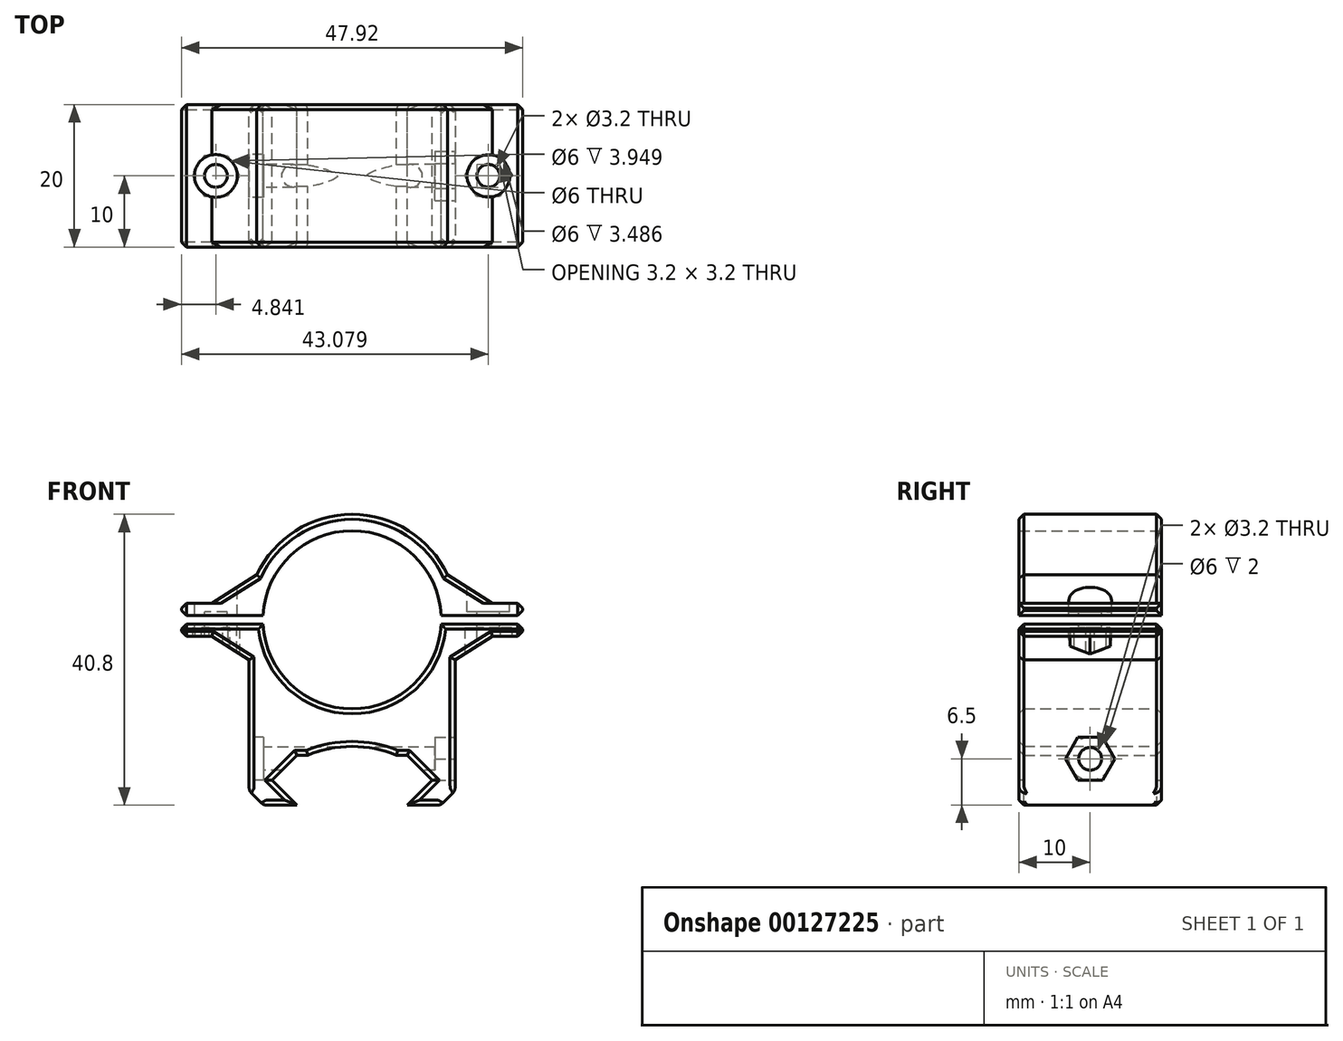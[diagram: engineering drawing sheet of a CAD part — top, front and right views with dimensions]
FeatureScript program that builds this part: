
annotation { "Feature Type Name" : "Feature", "Feature Type Description" : "" }
export const myFeature = defineFeature(function(context is Context, id is Id, definition is map)
    precondition{}
    {
        {
            var Q0;
            Q0=qCreatedBy(makeId("Front.planeOp"),FACE);
            var sketch = newSketch(context, id + "F0", { "sketchPlane" : qUnion([Q0])});
            skArc(sketch, "E0", {"start": v(0, -14.8) * mm, "mid": v(10.25, -10.67) * mm, "end": v(14.79, -0.6) * mm});
            skLineSegment(sketch, "E1.bottom", {"start": v(14.62, 2.3) * mm, "end": v(23.96, 2.3) * mm});
            skLineSegment(sketch, "E1.top", {"start": v(14.62, -2.3) * mm, "end": v(23.96, -2.3) * mm});
            skLineSegment(sketch, "E1.right", {"start": v(23.96, 2.3) * mm, "end": v(23.96, 0.6) * mm});
            skLineSegment(sketch, "E2", {"start": v(-7.75, -26) * mm, "end": v(-11.25, -22.5) * mm});
            skLineSegment(sketch, "E3.0", {"start": v(-14.45, -26) * mm, "end": v(-14.45, -14.6) * mm});
            skLineSegment(sketch, "E4.MirrorCS", {"start": v(7.75, -26) * mm, "end": v(11.25, -22.5) * mm});
            skLineSegment(sketch, "E5.MirrorCS", {"start": v(14.45, -26) * mm, "end": v(14.45, -23.8) * mm});
            skLineSegment(sketch, "E6.bottom", {"start": v(23.96, 0.6) * mm, "end": v(14.62, 0.6) * mm});
            skLineSegment(sketch, "E6.top", {"start": v(23.96, -0.6) * mm, "end": v(14.62, -0.6) * mm});
            skPoint(sketch, "E6.middle", {"position": v(19.29, 0) * mm});
            skLineSegment(sketch, "E7", {"start": v(-14.45, -3.2) * mm, "end": v(-14.45, -14.6) * mm});
            skLineSegment(sketch, "E8", {"start": v(14.45, -3.2) * mm, "end": v(14.45, -23.8) * mm});
            skLineSegment(sketch, "E9", {"start": v(-14.45, -26) * mm, "end": v(-7.75, -26) * mm});
            skLineSegment(sketch, "E10", {"start": v(7.75, -26) * mm, "end": v(14.45, -26) * mm});
            skLineSegment(sketch, "E11.trimOffspring", {"start": v(23.96, -0.6) * mm, "end": v(23.96, -2.3) * mm});
            skLineSegment(sketch, "E12", {"start": v(-7.75, -19) * mm, "end": v(-11.25, -22.5) * mm});
            skLineSegment(sketch, "E13.MirrorCS", {"start": v(7.75, -19) * mm, "end": v(11.25, -22.5) * mm});
            skArc(sketch, "E14", {"start": v(12.49, 0.6) * mm, "mid": v(-12.5, 0) * mm, "end": v(12.49, -0.6) * mm});
            skLineSegment(sketch, "E15", {"start": v(-7.75, -19) * mm, "end": v(0, -19) * mm});
            skLineSegment(sketch, "E16", {"start": v(0, -19) * mm, "end": v(0, -14.8) * mm});
            skLineSegment(sketch, "E17", {"start": v(7.75, -19) * mm, "end": v(0, -19) * mm});
            skLineSegment(sketch, "E18", {"start": v(0, -14.8) * mm, "end": v(0, -14.8) * mm});
            skLineSegment(sketch, "E19", {"start": v(14.62, 2.3) * mm, "end": v(12.29, 2.3) * mm});
            skLineSegment(sketch, "E20", {"start": v(14.62, 0.6) * mm, "end": v(12.49, 0.6) * mm});
            skLineSegment(sketch, "E21", {"start": v(14.62, -0.6) * mm, "end": v(12.49, -0.6) * mm});
            skLineSegment(sketch, "E22", {"start": v(14.62, -2.3) * mm, "end": v(12.29, -2.3) * mm});
            skArc(sketch, "E23.trimOffspring", {"start": v(14.79, 0.6) * mm, "mid": v(-10.67, 10.25) * mm, "end": v(0, -14.8) * mm});
            skLineSegment(sketch, "E24.MirrorCS", {"start": v(-14.62, 2.3) * mm, "end": v(-23.96, 2.3) * mm});
            skLineSegment(sketch, "E25.MirrorCS", {"start": v(-23.96, 2.3) * mm, "end": v(-23.96, 0.6) * mm});
            skLineSegment(sketch, "E26.MirrorCS", {"start": v(-23.96, 0.6) * mm, "end": v(-14.62, 0.6) * mm});
            skLineSegment(sketch, "E27.MirrorCS", {"start": v(-23.96, -0.6) * mm, "end": v(-14.62, -0.6) * mm});
            skLineSegment(sketch, "E28.MirrorCS", {"start": v(-14.62, -2.3) * mm, "end": v(-23.96, -2.3) * mm});
            skLineSegment(sketch, "E29.MirrorCS", {"start": v(-23.96, -0.6) * mm, "end": v(-23.96, -2.3) * mm});
            skLineSegment(sketch, "E30.MirrorCS", {"start": v(-14.62, 0.6) * mm, "end": v(-12.49, 0.6) * mm});
            skLineSegment(sketch, "E31.MirrorCS", {"start": v(-14.62, -0.6) * mm, "end": v(-12.49, -0.6) * mm});
            skPoint(sketch, "E32.orphan", {"position": v(14.45, -14.6) * mm});
            skArc(sketch, "E33", {"start": v(6.25, -19) * mm, "mid": v(0, -17.77) * mm, "end": v(-6.25, -19) * mm});
            skSolve(sketch);
        }
        {
            var Q0;
            Q0=makeQuery(id+"F0.imprint","IMPRINT",FACE,{"disambiguationData":[TD([[makeQuery(id+"F0.imprint","IMPRINT",EDGE,{"derivedFrom":sQuery(id+"F0.wireOp",EDGE,"E2")}),1.0]])]});
            var Q1;
            Q1=makeQuery(id+"F0.imprint","IMPRINT",FACE,{"disambiguationData":[TD([[makeQuery(id+"F0.imprint","IMPRINT",EDGE,{"derivedFrom":sQuery(id+"F0.wireOp",EDGE,"W4pV5Rjo-NDwQ-rgVk-bVmp-dATyTHXsbS4B")}),-1.0]])]});
            var Q2;
            Q2=makeQuery(id+"F0.imprint","IMPRINT",FACE,{"disambiguationData":[TD([[makeQuery(id+"F0.imprint","IMPRINT",EDGE,{"derivedFrom":sQuery(id+"F0.wireOp",EDGE,"E4.MirrorCS")}),-1.0]])]});
            var Q3;
            {var subQ0=sQuery(id+"F0.wireOp",EDGE,"E1.bottom");Q3=makeQuery(id+"F0.imprint","IMPRINT",FACE,{"disambiguationData":[TD([[makeQuery(id+"F0.imprint","IMPRINT",EDGE,{"derivedFrom":subQ0}),-1.0]])]});}
            var Q4;
            {var subQ0=sQuery(id+"F0.wireOp",EDGE,"E1.top");Q4=makeQuery(id+"F0.imprint","IMPRINT",FACE,{"disambiguationData":[TD([[makeQuery(id+"F0.imprint","IMPRINT",EDGE,{"derivedFrom":subQ0}),1.0]])]});}
            var Q5;
            Q5=makeQuery(id+"F0.imprint","IMPRINT",FACE,{"disambiguationData":[TD([[makeQuery(id+"F0.imprint","IMPRINT",EDGE,{"derivedFrom":sQuery(id+"F0.wireOp",EDGE,"E14")}),-1.0]])]});
            var Q6;
            {var subQ0=sQuery(id+"F0.wireOp",EDGE,"E18");Q6=makeQuery(id+"F0.imprint","IMPRINT",FACE,{"disambiguationData":[TD([[makeQuery(id+"F0.imprint","IMPRINT",EDGE,{"derivedFrom":subQ0}),-1.0]])]});}
            var Q7;
            {var subQ0=sQuery(id+"F0.wireOp",EDGE,"E19");Q7=makeQuery(id+"F0.imprint","IMPRINT",FACE,{"disambiguationData":[TD([[makeQuery(id+"F0.imprint","IMPRINT",EDGE,{"derivedFrom":subQ0}),-1.0]])]});}
            var Q8;
            {var subQ0=sQuery(id+"F0.wireOp",EDGE,"E22");Q8=makeQuery(id+"F0.imprint","IMPRINT",FACE,{"disambiguationData":[TD([[makeQuery(id+"F0.imprint","IMPRINT",EDGE,{"derivedFrom":subQ0}),1.0]])]});}
            var Q9;
            {var subQ0=sQuery(id+"F0.wireOp",EDGE,"E24.MirrorCS");Q9=makeQuery(id+"F0.imprint","IMPRINT",FACE,{"disambiguationData":[TD([[makeQuery(id+"F0.imprint","IMPRINT",EDGE,{"derivedFrom":subQ0}),1.0]])]});}
            var Q10;
            {var subQ0=sQuery(id+"F0.wireOp",EDGE,"E28.MirrorCS");Q10=makeQuery(id+"F0.imprint","IMPRINT",FACE,{"disambiguationData":[TD([[makeQuery(id+"F0.imprint","IMPRINT",EDGE,{"derivedFrom":subQ0}),-1.0]])]});}
            extrude(context, id + "F1", {"entities" : qUnion([Q0, Q1, Q2, Q3, Q4, Q5, Q6, Q7, Q8, Q9, Q10]), "depth" : 20 * mm});
        }
        {
            var Q0;
            Q0=makeQuery(id+"F1.opExtrude","SWEPT_FACE",FACE,{"disambiguationData":[OSD([sQuery(id+"F0.wireOp",EDGE,"E24.MirrorCS")])]});
            var sketch = newSketch(context, id + "F2", { "sketchPlane" : qUnion([Q0])});
            skCircle(sketch, "E34", {"center": v(19.12, -10) * mm, "radius": 1.6 * mm});
            skCircle(sketch, "E35", {"center": v(19.12, -10) * mm, "radius": 3 * mm});
            skCircle(sketch, "E36.MirrorC", {"center": v(-19.12, -10) * mm, "radius": 1.6 * mm});
            skCircle(sketch, "E37.MirrorC", {"center": v(-19.12, -10) * mm, "radius": 3 * mm});
            skLineSegment(sketch, "E38", {"start": v(-19.12, 0) * mm, "end": v(-19.12, -20) * mm, "construction": true});
            skSolve(sketch);
        }
        {
            var Q0;
            Q0=makeQuery(id+"F1.opExtrude","SWEPT_FACE",FACE,{"disambiguationData":[OSD([sQuery(id+"F0.wireOp",EDGE,"E7")])]});
            var sketch = newSketch(context, id + "F3", { "sketchPlane" : qUnion([Q0])});
            skCircle(sketch, "E39", {"center": v(10, -19.5) * mm, "radius": 1.6 * mm});
            skCircle(sketch, "E40", {"center": v(10, -19.5) * mm, "radius": 3 * mm});
            skLineSegment(sketch, "E41", {"start": v(0, -19.5) * mm, "end": v(20, -19.5) * mm});
            skSolve(sketch);
        }
        {
            var Q0;
            Q0=makeQuery(id+"F3.imprint","IMPRINT",FACE,{"disambiguationData":[TD([[makeQuery(id+"F3.imprint","IMPRINT",EDGE,{"derivedFrom":sQuery(id+"F3.wireOp",EDGE,"E39")}),1.0]])]});
            extrude(context, id + "F4", {"entities" : qUnion([Q0]), "operationType" : NewBodyOperationType.REMOVE, "oppositeDirection" : true, "depth" : 40 * mm});
        }
        {
            var Q0;
            Q0=makeQuery(id+"F2.imprint","IMPRINT",FACE,{"disambiguationData":[TD([[makeQuery(id+"F2.imprint","IMPRINT",EDGE,{"derivedFrom":sQuery(id+"F2.wireOp",EDGE,"E34")}),1.0]])]});
            var Q1;
            Q1=makeQuery(id+"F2.imprint","IMPRINT",FACE,{"disambiguationData":[TD([[makeQuery(id+"F2.imprint","IMPRINT",EDGE,{"derivedFrom":sQuery(id+"F2.wireOp",EDGE,"E36.MirrorC")}),-1.0]])]});
            extrude(context, id + "F5", {"entities" : qUnion([Q0, Q1]), "operationType" : NewBodyOperationType.REMOVE, "oppositeDirection" : true, "depth" : 25 * mm});
        }
        {
            var Q0;
            Q0=qSketchRegion(id+"F3",true);
            var Q1;
            {var subQ0=sQuery(id+"F3.wireOp",EDGE,"E41");var subQ1=sQuery(id+"F3.wireOp",EDGE,"E39");var subQ2=makeQuery(id+"F3.imprint","INTERSECT",VERTEX,{"disambiguationData":[OD(0.0)],"derivedFrom":[subQ1,subQ0]});Q1=makeQuery(id+"F3.imprint","IMPRINT",FACE,{"disambiguationData":[TD([[makeQuery(id+"F3.imprint","IMPRINT",EDGE,{"disambiguationData":[TD([[subQ2,1.0]])],"derivedFrom":subQ1}),-1.0]])]});}
            extrude(context, id + "F6", {"entities" : qUnion([Q0, Q1]), "operationType" : NewBodyOperationType.REMOVE, "oppositeDirection" : true, "depth" : 2 * mm});
        }
        {
            var Q0;
            Q0=makeQuery(id+"F1.opExtrude","SWEPT_FACE",FACE,{"disambiguationData":[OSD([sQuery(id+"F0.wireOp",EDGE,"E8")])]});
            var sketch = newSketch(context, id + "F7", { "sketchPlane" : qUnion([Q0])});
            skCircle(sketch, "E42.cCircle", {"center": v(-10, -19.5) * mm, "radius": 3 * mm, "construction": true});
            skLineSegment(sketch, "E42.0", {"start": v(-8.27, -22.5) * mm, "end": v(-11.73, -22.5) * mm});
            skLineSegment(sketch, "E42.1", {"start": v(-11.73, -22.5) * mm, "end": v(-13.46, -19.5) * mm});
            skLineSegment(sketch, "E42.2", {"start": v(-13.46, -19.5) * mm, "end": v(-11.73, -16.5) * mm});
            skLineSegment(sketch, "E42.3", {"start": v(-11.73, -16.5) * mm, "end": v(-8.27, -16.5) * mm});
            skLineSegment(sketch, "E42.4", {"start": v(-8.27, -16.5) * mm, "end": v(-6.54, -19.5) * mm});
            skLineSegment(sketch, "E42.5", {"start": v(-6.54, -19.5) * mm, "end": v(-8.27, -22.5) * mm});
            skPoint(sketch, "E42.0.midPoint", {"position": v(-10, -22.5) * mm});
            skLineSegment(sketch, "E43", {"start": v(-20, -19.5) * mm, "end": v(0, -19.5) * mm, "construction": true});
            skSolve(sketch);
        }
        {
            var Q0;
            Q0=makeQuery(id+"F2.imprint","IMPRINT",FACE,{"disambiguationData":[TD([[makeQuery(id+"F2.imprint","IMPRINT",EDGE,{"derivedFrom":sQuery(id+"F2.wireOp",EDGE,"E34")}),-1.0]])]});
            var Q1;
            Q1=makeQuery(id+"F2.imprint","IMPRINT",FACE,{"disambiguationData":[TD([[makeQuery(id+"F2.imprint","IMPRINT",EDGE,{"derivedFrom":sQuery(id+"F2.wireOp",EDGE,"E36.MirrorC")}),1.0]])]});
            extrude(context, id + "F8", {"entities" : qUnion([Q0, Q1]), "operationType" : NewBodyOperationType.REMOVE, "oppositeDirection" : true, "depth" : 1.2 * mm});
        }
        {
            var Q0;
            Q0=makeQuery(id+"F1.opExtrude","SWEPT_FACE",FACE,{"disambiguationData":[OSD([sQuery(id+"F0.wireOp",EDGE,"E1.top")])]});
            var sketch = newSketch(context, id + "F9", { "sketchPlane" : qUnion([Q0])});
            skCircle(sketch, "E44.cCircle", {"center": v(19.12, 10) * mm, "radius": 2.85 * mm, "construction": true});
            skLineSegment(sketch, "E44.0", {"start": v(20.76, 7.15) * mm, "end": v(17.47, 7.15) * mm});
            skLineSegment(sketch, "E44.1", {"start": v(17.47, 7.15) * mm, "end": v(15.83, 10) * mm});
            skLineSegment(sketch, "E44.2", {"start": v(15.83, 10) * mm, "end": v(17.47, 12.85) * mm});
            skLineSegment(sketch, "E44.3", {"start": v(17.47, 12.85) * mm, "end": v(20.76, 12.85) * mm});
            skLineSegment(sketch, "E44.4", {"start": v(20.76, 12.85) * mm, "end": v(22.4, 10) * mm});
            skLineSegment(sketch, "E44.5", {"start": v(22.4, 10) * mm, "end": v(20.76, 7.15) * mm});
            skPoint(sketch, "E44.0.midPoint", {"position": v(19.12, 7.15) * mm});
            skCircle(sketch, "E45", {"center": v(19.12, 10) * mm, "radius": 1.6 * mm});
            skCircle(sketch, "E46.cCircle", {"center": v(-19.12, 10) * mm, "radius": 2.85 * mm, "construction": true});
            skLineSegment(sketch, "E46.0", {"start": v(-15.83, 10) * mm, "end": v(-17.47, 7.15) * mm});
            skLineSegment(sketch, "E46.1", {"start": v(-17.47, 7.15) * mm, "end": v(-20.76, 7.15) * mm});
            skLineSegment(sketch, "E46.2", {"start": v(-20.76, 7.15) * mm, "end": v(-22.4, 10) * mm});
            skLineSegment(sketch, "E46.3", {"start": v(-22.4, 10) * mm, "end": v(-20.76, 12.85) * mm});
            skLineSegment(sketch, "E46.4", {"start": v(-20.76, 12.85) * mm, "end": v(-17.47, 12.85) * mm});
            skLineSegment(sketch, "E46.5", {"start": v(-17.47, 12.85) * mm, "end": v(-15.83, 10) * mm});
            skPoint(sketch, "E46.0.midPoint", {"position": v(-16.65, 8.57) * mm});
            skLineSegment(sketch, "E47.0", {"start": v(-19.12, 0) * mm, "end": v(-19.12, 20) * mm, "construction": true});
            skSolve(sketch);
        }
        {
            var Q0;
            Q0=makeQuery(id+"F1.opExtrude","SWEPT_EDGE",EDGE,{"disambiguationData":[OSD([sQuery(id+"F0.wireOp",EDGE,"E1.bottom"),sQuery(id+"F0.wireOp",EDGE,"E19"),sQuery(id+"F0.wireOp",EDGE,"E23.trimOffspring")])]});
            var Q1;
            Q1=makeQuery(id+"F1.opExtrude","SWEPT_EDGE",EDGE,{"disambiguationData":[OSD([sQuery(id+"F0.wireOp",EDGE,"E0"),sQuery(id+"F0.wireOp",EDGE,"E1.top"),sQuery(id+"F0.wireOp",EDGE,"E22")])]});
            var Q2;
            Q2=makeQuery(id+"F1.opExtrude","SWEPT_EDGE",EDGE,{"disambiguationData":[OSD([sQuery(id+"F0.wireOp",EDGE,"E23.trimOffspring"),sQuery(id+"F0.wireOp",EDGE,"E24.MirrorCS")])]});
            var Q3;
            Q3=makeQuery(id+"F1.opExtrude","SWEPT_EDGE",EDGE,{"disambiguationData":[OSD([sQuery(id+"F0.wireOp",EDGE,"E23.trimOffspring"),sQuery(id+"F0.wireOp",EDGE,"E28.MirrorCS")])]});
            chamfer(context, id + "F10", {"entities" : qUnion([Q0, Q1, Q2, Q3]), "width" : 7 * mm, "tangentPropagation" : true});
        }
        {
            var Q0;
            Q0=makeQuery(id+"F1.opExtrude","CAP_FACE",FACE,{"disambiguationData":[OSD([sQuery(id+"F0.wireOp",EDGE,"E0"),sQuery(id+"F0.wireOp",EDGE,"E1.bottom"),sQuery(id+"F0.wireOp",EDGE,"E1.top"),sQuery(id+"F0.wireOp",EDGE,"E1.right"),sQuery(id+"F0.wireOp",EDGE,"E2"),sQuery(id+"F0.wireOp",EDGE,"E3.0"),sQuery(id+"F0.wireOp",EDGE,"E4.MirrorCS"),sQuery(id+"F0.wireOp",EDGE,"E5.MirrorCS"),sQuery(id+"F0.wireOp",EDGE,"E6.bottom"),sQuery(id+"F0.wireOp",EDGE,"E6.top"),sQuery(id+"F0.wireOp",EDGE,"E7"),sQuery(id+"F0.wireOp",EDGE,"E8"),sQuery(id+"F0.wireOp",EDGE,"E9"),sQuery(id+"F0.wireOp",EDGE,"E10"),sQuery(id+"F0.wireOp",EDGE,"E11.trimOffspring"),sQuery(id+"F0.wireOp",EDGE,"E12"),sQuery(id+"F0.wireOp",EDGE,"E13.MirrorCS"),sQuery(id+"F0.wireOp",EDGE,"E14"),sQuery(id+"F0.wireOp",EDGE,"E15"),sQuery(id+"F0.wireOp",EDGE,"E17"),sQuery(id+"F0.wireOp",EDGE,"E20"),sQuery(id+"F0.wireOp",EDGE,"E21"),sQuery(id+"F0.wireOp",EDGE,"E23.trimOffspring"),sQuery(id+"F0.wireOp",EDGE,"E24.MirrorCS"),sQuery(id+"F0.wireOp",EDGE,"E25.MirrorCS"),sQuery(id+"F0.wireOp",EDGE,"E26.MirrorCS"),sQuery(id+"F0.wireOp",EDGE,"E27.MirrorCS"),sQuery(id+"F0.wireOp",EDGE,"E28.MirrorCS"),sQuery(id+"F0.wireOp",EDGE,"E29.MirrorCS")])],"isStart":false});
            var sketch = newSketch(context, id + "F11", { "sketchPlane" : qUnion([Q0])});
            skLineSegment(sketch, "E48.bottom", {"start": v(-23.96, 0.6) * mm, "end": v(-20.41, 0.6) * mm});
            skLineSegment(sketch, "E48.top", {"start": v(-23.96, -0.6) * mm, "end": v(-20.41, -0.6) * mm});
            skLineSegment(sketch, "E48.left", {"start": v(-23.96, 0.6) * mm, "end": v(-23.96, -0.6) * mm});
            skLineSegment(sketch, "E48.right", {"start": v(-20.41, 0.6) * mm, "end": v(-20.41, -0.6) * mm});
            skSolve(sketch);
        }
        {
            var Q0;
            {var subQ0=sQuery(id+"F11.wireOp",EDGE,"E48.right");Q0=makeQuery(id+"F11.imprint","IMPRINT",FACE,{"disambiguationData":[TD([[makeQuery(id+"F11.imprint","IMPRINT",EDGE,{"derivedFrom":subQ0}),-1.0]])]});}
            var Q1;
            {var subQ0=sQuery(id+"F11.wireOp",EDGE,"E48.left");Q1=makeQuery(id+"F11.imprint","IMPRINT",FACE,{"disambiguationData":[TD([[makeQuery(id+"F11.imprint","IMPRINT",EDGE,{"derivedFrom":subQ0}),1.0]])]});}
            extrude(context, id + "F12", {"entities" : qUnion([Q0, Q1]), "operationType" : NewBodyOperationType.REMOVE, "endBound" : BoundingType.THROUGH_ALL, "oppositeDirection" : true, "depth" : 25 * mm});
        }
        {
            var Q0;
            Q0=qSketchRegion(id+"F9",true);
            extrude(context, id + "F13", {"entities" : qUnion([Q0]), "operationType" : NewBodyOperationType.REMOVE, "oppositeDirection" : true, "depth" : 1.2 * mm, "hasSecondDirection" : true, "secondDirectionOppositeDirection" : false, "secondDirectionDepth" : 25 * mm});
        }
        {
            var Q0;
            Q0=qSketchRegion(id+"F7",true);
            extrude(context, id + "F14", {"entities" : qUnion([Q0]), "operationType" : NewBodyOperationType.REMOVE, "oppositeDirection" : true, "depth" : 2.8 * mm});
        }
        {
            var Q0;
            Q0=makeQuery(id+"F1.opExtrude","CAP_EDGE",EDGE,{"disambiguationData":[OSD([sQuery(id+"F0.wireOp",EDGE,"E5.MirrorCS"),sQuery(id+"F0.wireOp",EDGE,"E8")])],"isStart":false});
            var Q1;
            {var subQ0=sQuery(id+"F0.wireOp",EDGE,"E33");var subQ1=sQuery(id+"F0.wireOp",EDGE,"E29.MirrorCS");var subQ2=sQuery(id+"F0.wireOp",EDGE,"E28.MirrorCS");var subQ3=sQuery(id+"F0.wireOp",EDGE,"E14");var subQ4=sQuery(id+"F0.wireOp",EDGE,"E17");var subQ5=sQuery(id+"F0.wireOp",EDGE,"E23.trimOffspring");var subQ6=sQuery(id+"F0.wireOp",EDGE,"E7");var subQ7=sQuery(id+"F0.wireOp",EDGE,"E11.trimOffspring");var subQ8=sQuery(id+"F0.wireOp",EDGE,"E12");var subQ9=sQuery(id+"F0.wireOp",EDGE,"E3.0");var subQ10=sQuery(id+"F0.wireOp",EDGE,"E2");var subQ11=sQuery(id+"F0.wireOp",EDGE,"E1.top");var subQ12=sQuery(id+"F0.wireOp",EDGE,"E27.MirrorCS");var subQ13=sQuery(id+"F0.wireOp",EDGE,"E0");var subQ14=sQuery(id+"F0.wireOp",EDGE,"E4.MirrorCS");var subQ15=sQuery(id+"F0.wireOp",EDGE,"E13.MirrorCS");var subQ16=sQuery(id+"F0.wireOp",EDGE,"E8");var subQ17=sQuery(id+"F0.wireOp",EDGE,"E5.MirrorCS");var subQ18=sQuery(id+"F0.wireOp",EDGE,"E15");var subQ19=sQuery(id+"F0.wireOp",EDGE,"E21");var subQ20=sQuery(id+"F0.wireOp",EDGE,"E6.top");var subQ21=sQuery(id+"F0.wireOp",EDGE,"E9");var subQ22=sQuery(id+"F0.wireOp",EDGE,"E10");Q1=makeQuery(id+"F12.boolean.opBoolean","SPLIT",FACE,{"disambiguationData":[TD([makeQuery(id+"F1.opExtrude","SWEPT_FACE",FACE,{"disambiguationData":[OSD([subQ13])]})])],"derivedFrom":makeQuery(id+"F1.opExtrude","CAP_FACE",FACE,{"disambiguationData":[OSD([subQ13,sQuery(id+"F0.wireOp",EDGE,"E1.bottom"),subQ11,sQuery(id+"F0.wireOp",EDGE,"E1.right"),subQ10,subQ9,subQ14,subQ17,sQuery(id+"F0.wireOp",EDGE,"E6.bottom"),subQ20,subQ6,subQ16,subQ21,subQ22,subQ7,subQ8,subQ15,subQ3,subQ18,subQ4,sQuery(id+"F0.wireOp",EDGE,"E20"),subQ19,subQ5,sQuery(id+"F0.wireOp",EDGE,"E24.MirrorCS"),sQuery(id+"F0.wireOp",EDGE,"E25.MirrorCS"),sQuery(id+"F0.wireOp",EDGE,"E26.MirrorCS"),subQ12,subQ2,subQ1,subQ0])],"isStart":false})});}
            var Q2;
            {var subQ0=sQuery(id+"F0.wireOp",EDGE,"E24.MirrorCS");var subQ1=sQuery(id+"F0.wireOp",EDGE,"E23.trimOffspring");var subQ3=sQuery(id+"F0.wireOp",EDGE,"E1.bottom");var subQ4=sQuery(id+"F0.wireOp",EDGE,"E26.MirrorCS");var subQ5=sQuery(id+"F0.wireOp",EDGE,"E25.MirrorCS");var subQ6=sQuery(id+"F0.wireOp",EDGE,"E14");var subQ7=sQuery(id+"F0.wireOp",EDGE,"E20");var subQ8=sQuery(id+"F0.wireOp",EDGE,"E6.bottom");var subQ9=sQuery(id+"F0.wireOp",EDGE,"E1.right");Q2=makeQuery(id+"F12.boolean.opBoolean","SPLIT",FACE,{"disambiguationData":[TD([makeQuery(id+"F1.opExtrude","SWEPT_FACE",FACE,{"disambiguationData":[OSD([subQ3])]})])],"derivedFrom":makeQuery(id+"F1.opExtrude","CAP_FACE",FACE,{"disambiguationData":[OSD([sQuery(id+"F0.wireOp",EDGE,"E0"),subQ3,sQuery(id+"F0.wireOp",EDGE,"E1.top"),subQ9,sQuery(id+"F0.wireOp",EDGE,"E2"),sQuery(id+"F0.wireOp",EDGE,"E3.0"),sQuery(id+"F0.wireOp",EDGE,"E4.MirrorCS"),sQuery(id+"F0.wireOp",EDGE,"E5.MirrorCS"),subQ8,sQuery(id+"F0.wireOp",EDGE,"E6.top"),sQuery(id+"F0.wireOp",EDGE,"E7"),sQuery(id+"F0.wireOp",EDGE,"E8"),sQuery(id+"F0.wireOp",EDGE,"E9"),sQuery(id+"F0.wireOp",EDGE,"E10"),sQuery(id+"F0.wireOp",EDGE,"E11.trimOffspring"),sQuery(id+"F0.wireOp",EDGE,"E12"),sQuery(id+"F0.wireOp",EDGE,"E13.MirrorCS"),subQ6,sQuery(id+"F0.wireOp",EDGE,"E15"),sQuery(id+"F0.wireOp",EDGE,"E17"),subQ7,sQuery(id+"F0.wireOp",EDGE,"E21"),subQ1,subQ0,subQ5,subQ4,sQuery(id+"F0.wireOp",EDGE,"E27.MirrorCS"),sQuery(id+"F0.wireOp",EDGE,"E28.MirrorCS"),sQuery(id+"F0.wireOp",EDGE,"E29.MirrorCS"),sQuery(id+"F0.wireOp",EDGE,"E33")])],"isStart":false})});}
            var Q3;
            {var subQ0=sQuery(id+"F0.wireOp",EDGE,"E24.MirrorCS");var subQ1=sQuery(id+"F0.wireOp",EDGE,"E23.trimOffspring");var subQ3=sQuery(id+"F0.wireOp",EDGE,"E1.bottom");var subQ4=sQuery(id+"F0.wireOp",EDGE,"E26.MirrorCS");var subQ5=sQuery(id+"F0.wireOp",EDGE,"E25.MirrorCS");var subQ6=sQuery(id+"F0.wireOp",EDGE,"E14");var subQ7=sQuery(id+"F0.wireOp",EDGE,"E20");var subQ8=sQuery(id+"F0.wireOp",EDGE,"E6.bottom");var subQ9=sQuery(id+"F0.wireOp",EDGE,"E1.right");Q3=makeQuery(id+"F12.boolean.opBoolean","SPLIT",FACE,{"disambiguationData":[TD([makeQuery(id+"F1.opExtrude","SWEPT_FACE",FACE,{"disambiguationData":[OSD([subQ3])]})])],"derivedFrom":makeQuery(id+"F1.opExtrude","CAP_FACE",FACE,{"disambiguationData":[OSD([sQuery(id+"F0.wireOp",EDGE,"E0"),subQ3,sQuery(id+"F0.wireOp",EDGE,"E1.top"),subQ9,sQuery(id+"F0.wireOp",EDGE,"E2"),sQuery(id+"F0.wireOp",EDGE,"E3.0"),sQuery(id+"F0.wireOp",EDGE,"E4.MirrorCS"),sQuery(id+"F0.wireOp",EDGE,"E5.MirrorCS"),subQ8,sQuery(id+"F0.wireOp",EDGE,"E6.top"),sQuery(id+"F0.wireOp",EDGE,"E7"),sQuery(id+"F0.wireOp",EDGE,"E8"),sQuery(id+"F0.wireOp",EDGE,"E9"),sQuery(id+"F0.wireOp",EDGE,"E10"),sQuery(id+"F0.wireOp",EDGE,"E11.trimOffspring"),sQuery(id+"F0.wireOp",EDGE,"E12"),sQuery(id+"F0.wireOp",EDGE,"E13.MirrorCS"),subQ6,sQuery(id+"F0.wireOp",EDGE,"E15"),sQuery(id+"F0.wireOp",EDGE,"E17"),subQ7,sQuery(id+"F0.wireOp",EDGE,"E21"),subQ1,subQ0,subQ5,subQ4,sQuery(id+"F0.wireOp",EDGE,"E27.MirrorCS"),sQuery(id+"F0.wireOp",EDGE,"E28.MirrorCS"),sQuery(id+"F0.wireOp",EDGE,"E29.MirrorCS"),sQuery(id+"F0.wireOp",EDGE,"E33")])],"isStart":true})});}
            var Q4;
            {var subQ0=sQuery(id+"F0.wireOp",EDGE,"E33");var subQ1=sQuery(id+"F0.wireOp",EDGE,"E29.MirrorCS");var subQ2=sQuery(id+"F0.wireOp",EDGE,"E28.MirrorCS");var subQ3=sQuery(id+"F0.wireOp",EDGE,"E14");var subQ4=sQuery(id+"F0.wireOp",EDGE,"E17");var subQ5=sQuery(id+"F0.wireOp",EDGE,"E23.trimOffspring");var subQ6=sQuery(id+"F0.wireOp",EDGE,"E7");var subQ7=sQuery(id+"F0.wireOp",EDGE,"E11.trimOffspring");var subQ8=sQuery(id+"F0.wireOp",EDGE,"E12");var subQ9=sQuery(id+"F0.wireOp",EDGE,"E3.0");var subQ10=sQuery(id+"F0.wireOp",EDGE,"E2");var subQ11=sQuery(id+"F0.wireOp",EDGE,"E1.top");var subQ12=sQuery(id+"F0.wireOp",EDGE,"E27.MirrorCS");var subQ13=sQuery(id+"F0.wireOp",EDGE,"E0");var subQ14=sQuery(id+"F0.wireOp",EDGE,"E4.MirrorCS");var subQ15=sQuery(id+"F0.wireOp",EDGE,"E13.MirrorCS");var subQ16=sQuery(id+"F0.wireOp",EDGE,"E8");var subQ17=sQuery(id+"F0.wireOp",EDGE,"E5.MirrorCS");var subQ18=sQuery(id+"F0.wireOp",EDGE,"E15");var subQ19=sQuery(id+"F0.wireOp",EDGE,"E21");var subQ20=sQuery(id+"F0.wireOp",EDGE,"E6.top");var subQ21=sQuery(id+"F0.wireOp",EDGE,"E9");var subQ22=sQuery(id+"F0.wireOp",EDGE,"E10");Q4=makeQuery(id+"F12.boolean.opBoolean","SPLIT",FACE,{"disambiguationData":[TD([makeQuery(id+"F1.opExtrude","SWEPT_FACE",FACE,{"disambiguationData":[OSD([subQ13])]})])],"derivedFrom":makeQuery(id+"F1.opExtrude","CAP_FACE",FACE,{"disambiguationData":[OSD([subQ13,sQuery(id+"F0.wireOp",EDGE,"E1.bottom"),subQ11,sQuery(id+"F0.wireOp",EDGE,"E1.right"),subQ10,subQ9,subQ14,subQ17,sQuery(id+"F0.wireOp",EDGE,"E6.bottom"),subQ20,subQ6,subQ16,subQ21,subQ22,subQ7,subQ8,subQ15,subQ3,subQ18,subQ4,sQuery(id+"F0.wireOp",EDGE,"E20"),subQ19,subQ5,sQuery(id+"F0.wireOp",EDGE,"E24.MirrorCS"),sQuery(id+"F0.wireOp",EDGE,"E25.MirrorCS"),sQuery(id+"F0.wireOp",EDGE,"E26.MirrorCS"),subQ12,subQ2,subQ1,subQ0])],"isStart":true})});}
            var Q5;
            Q5=makeQuery(id+"F1.opExtrude","SWEPT_FACE",FACE,{"disambiguationData":[OSD([sQuery(id+"F0.wireOp",EDGE,"E1.right")])]});
            var Q6;
            Q6=makeQuery(id+"F1.opExtrude","SWEPT_FACE",FACE,{"disambiguationData":[OSD([sQuery(id+"F0.wireOp",EDGE,"E11.trimOffspring")])]});
            var Q7;
            Q7=makeQuery(id+"F1.opExtrude","SWEPT_FACE",FACE,{"disambiguationData":[OSD([sQuery(id+"F0.wireOp",EDGE,"E25.MirrorCS")])]});
            var Q8;
            Q8=makeQuery(id+"F1.opExtrude","SWEPT_FACE",FACE,{"disambiguationData":[OSD([sQuery(id+"F0.wireOp",EDGE,"E29.MirrorCS")])]});
            var Q9;
            {var subQ0=sQuery(id+"F0.wireOp",EDGE,"E24.MirrorCS");var subQ1=sQuery(id+"F0.wireOp",EDGE,"E23.trimOffspring");Q9=makeQuery(id+"F10.opChamfer","BLEND_EDGE",EDGE,{"blendedFrom":[makeQuery(id+"F1.opExtrude","SWEPT_EDGE",EDGE,{"disambiguationData":[OSD([subQ1,subQ0])]}),makeQuery(id+"F1.opExtrude","CAP_FACE",FACE,{"disambiguationData":[OSD([sQuery(id+"F0.wireOp",EDGE,"E1.bottom"),sQuery(id+"F0.wireOp",EDGE,"E1.right"),sQuery(id+"F0.wireOp",EDGE,"E6.bottom"),sQuery(id+"F0.wireOp",EDGE,"E14"),sQuery(id+"F0.wireOp",EDGE,"E20"),subQ1,subQ0,sQuery(id+"F0.wireOp",EDGE,"E25.MirrorCS"),sQuery(id+"F0.wireOp",EDGE,"E26.MirrorCS"),sQuery(id+"F0.wireOp",EDGE,"E30.MirrorCS")])],"isStart":false})],"blendedInto":[makeQuery(id+"F1.opExtrude","CAP_FACE",FACE,{"disambiguationData":[OSD([sQuery(id+"F0.wireOp",EDGE,"E1.bottom"),sQuery(id+"F0.wireOp",EDGE,"E1.right"),sQuery(id+"F0.wireOp",EDGE,"E6.bottom"),sQuery(id+"F0.wireOp",EDGE,"E14"),sQuery(id+"F0.wireOp",EDGE,"E20"),subQ1,subQ0,sQuery(id+"F0.wireOp",EDGE,"E25.MirrorCS"),sQuery(id+"F0.wireOp",EDGE,"E26.MirrorCS"),sQuery(id+"F0.wireOp",EDGE,"E30.MirrorCS")])],"isStart":false})]});}
            var Q10;
            {var subQ0=sQuery(id+"F0.wireOp",EDGE,"E23.trimOffspring");Q10=makeQuery(id+"F1.opExtrude","CAP_EDGE",EDGE,{"disambiguationData":[OSD([subQ0]),TDD([makeQuery(id+"F0.imprint","IMPRINT",EDGE,{"disambiguationData":[TD([[makeQuery(id+"F0.imprint","INTERSECT",VERTEX,{"derivedFrom":[subQ0,sQuery(id+"F0.wireOp",EDGE,"E24.MirrorCS")]}),1.0]])],"derivedFrom":subQ0})])],"isStart":false});}
            var Q11;
            {var subQ0=sQuery(id+"F0.wireOp",EDGE,"E23.trimOffspring");var subQ1=sQuery(id+"F0.wireOp",EDGE,"E1.bottom");Q11=makeQuery(id+"F10.opChamfer","BLEND_EDGE",EDGE,{"blendedFrom":[makeQuery(id+"F1.opExtrude","SWEPT_EDGE",EDGE,{"disambiguationData":[OSD([subQ1,sQuery(id+"F0.wireOp",EDGE,"E19"),subQ0])]}),makeQuery(id+"F1.opExtrude","CAP_FACE",FACE,{"disambiguationData":[OSD([subQ1,sQuery(id+"F0.wireOp",EDGE,"E1.right"),sQuery(id+"F0.wireOp",EDGE,"E6.bottom"),sQuery(id+"F0.wireOp",EDGE,"E14"),sQuery(id+"F0.wireOp",EDGE,"E20"),subQ0,sQuery(id+"F0.wireOp",EDGE,"E24.MirrorCS"),sQuery(id+"F0.wireOp",EDGE,"E25.MirrorCS"),sQuery(id+"F0.wireOp",EDGE,"E26.MirrorCS"),sQuery(id+"F0.wireOp",EDGE,"E30.MirrorCS")])],"isStart":false})],"blendedInto":[makeQuery(id+"F1.opExtrude","CAP_FACE",FACE,{"disambiguationData":[OSD([subQ1,sQuery(id+"F0.wireOp",EDGE,"E1.right"),sQuery(id+"F0.wireOp",EDGE,"E6.bottom"),sQuery(id+"F0.wireOp",EDGE,"E14"),sQuery(id+"F0.wireOp",EDGE,"E20"),subQ0,sQuery(id+"F0.wireOp",EDGE,"E24.MirrorCS"),sQuery(id+"F0.wireOp",EDGE,"E25.MirrorCS"),sQuery(id+"F0.wireOp",EDGE,"E26.MirrorCS"),sQuery(id+"F0.wireOp",EDGE,"E30.MirrorCS")])],"isStart":false})]});}
            var Q12;
            {var subQ0=sQuery(id+"F0.wireOp",EDGE,"E24.MirrorCS");var subQ1=sQuery(id+"F0.wireOp",EDGE,"E23.trimOffspring");Q12=makeQuery(id+"F10.opChamfer","BLEND_EDGE",EDGE,{"blendedFrom":[makeQuery(id+"F1.opExtrude","SWEPT_EDGE",EDGE,{"disambiguationData":[OSD([subQ1,subQ0])]}),makeQuery(id+"F1.opExtrude","CAP_FACE",FACE,{"disambiguationData":[OSD([sQuery(id+"F0.wireOp",EDGE,"E1.bottom"),sQuery(id+"F0.wireOp",EDGE,"E1.right"),sQuery(id+"F0.wireOp",EDGE,"E6.bottom"),sQuery(id+"F0.wireOp",EDGE,"E14"),sQuery(id+"F0.wireOp",EDGE,"E20"),subQ1,subQ0,sQuery(id+"F0.wireOp",EDGE,"E25.MirrorCS"),sQuery(id+"F0.wireOp",EDGE,"E26.MirrorCS"),sQuery(id+"F0.wireOp",EDGE,"E30.MirrorCS")])],"isStart":true})],"blendedInto":[makeQuery(id+"F1.opExtrude","CAP_FACE",FACE,{"disambiguationData":[OSD([sQuery(id+"F0.wireOp",EDGE,"E1.bottom"),sQuery(id+"F0.wireOp",EDGE,"E1.right"),sQuery(id+"F0.wireOp",EDGE,"E6.bottom"),sQuery(id+"F0.wireOp",EDGE,"E14"),sQuery(id+"F0.wireOp",EDGE,"E20"),subQ1,subQ0,sQuery(id+"F0.wireOp",EDGE,"E25.MirrorCS"),sQuery(id+"F0.wireOp",EDGE,"E26.MirrorCS"),sQuery(id+"F0.wireOp",EDGE,"E30.MirrorCS")])],"isStart":true})]});}
            var Q13;
            {var subQ0=sQuery(id+"F0.wireOp",EDGE,"E23.trimOffspring");Q13=makeQuery(id+"F1.opExtrude","CAP_EDGE",EDGE,{"disambiguationData":[OSD([subQ0]),TDD([makeQuery(id+"F0.imprint","IMPRINT",EDGE,{"disambiguationData":[TD([[makeQuery(id+"F0.imprint","INTERSECT",VERTEX,{"derivedFrom":[subQ0,sQuery(id+"F0.wireOp",EDGE,"E24.MirrorCS")]}),1.0]])],"derivedFrom":subQ0})])],"isStart":true});}
            var Q14;
            {var subQ0=sQuery(id+"F0.wireOp",EDGE,"E23.trimOffspring");var subQ1=sQuery(id+"F0.wireOp",EDGE,"E1.bottom");Q14=makeQuery(id+"F10.opChamfer","BLEND_EDGE",EDGE,{"blendedFrom":[makeQuery(id+"F1.opExtrude","SWEPT_EDGE",EDGE,{"disambiguationData":[OSD([subQ1,sQuery(id+"F0.wireOp",EDGE,"E19"),subQ0])]}),makeQuery(id+"F1.opExtrude","CAP_FACE",FACE,{"disambiguationData":[OSD([subQ1,sQuery(id+"F0.wireOp",EDGE,"E1.right"),sQuery(id+"F0.wireOp",EDGE,"E6.bottom"),sQuery(id+"F0.wireOp",EDGE,"E14"),sQuery(id+"F0.wireOp",EDGE,"E20"),subQ0,sQuery(id+"F0.wireOp",EDGE,"E24.MirrorCS"),sQuery(id+"F0.wireOp",EDGE,"E25.MirrorCS"),sQuery(id+"F0.wireOp",EDGE,"E26.MirrorCS"),sQuery(id+"F0.wireOp",EDGE,"E30.MirrorCS")])],"isStart":true})],"blendedInto":[makeQuery(id+"F1.opExtrude","CAP_FACE",FACE,{"disambiguationData":[OSD([subQ1,sQuery(id+"F0.wireOp",EDGE,"E1.right"),sQuery(id+"F0.wireOp",EDGE,"E6.bottom"),sQuery(id+"F0.wireOp",EDGE,"E14"),sQuery(id+"F0.wireOp",EDGE,"E20"),subQ0,sQuery(id+"F0.wireOp",EDGE,"E24.MirrorCS"),sQuery(id+"F0.wireOp",EDGE,"E25.MirrorCS"),sQuery(id+"F0.wireOp",EDGE,"E26.MirrorCS"),sQuery(id+"F0.wireOp",EDGE,"E30.MirrorCS")])],"isStart":true})]});}
            chamfer(context, id + "F15", {"entities" : qUnion([Q0, Q1, Q2, Q3, Q4, Q5, Q6, Q7, Q8, Q9, Q10, Q11, Q12, Q13, Q14]), "width" : 0.7 * mm, "tangentPropagation" : true});
        }
        {
            var Q0;
            Q0=makeQuery(id+"F1.opExtrude","SWEPT_EDGE",EDGE,{"disambiguationData":[OSD([sQuery(id+"F0.wireOp",EDGE,"E5.MirrorCS"),sQuery(id+"F0.wireOp",EDGE,"E10")])]});
            var Q1;
            Q1=makeQuery(id+"F1.opExtrude","SWEPT_EDGE",EDGE,{"disambiguationData":[OSD([sQuery(id+"F0.wireOp",EDGE,"E3.0"),sQuery(id+"F0.wireOp",EDGE,"E9")])]});
            chamfer(context, id + "F16", {"entities" : qUnion([Q0, Q1]), "width" : 2 * mm, "tangentPropagation" : true});
        }
        {
            var Q0;
            Q0=makeQuery(id+"F16.opChamfer","BLEND_FACE",FACE,{"disambiguationData":[OSD([sQuery(id+"F0.wireOp",EDGE,"E3.0"),sQuery(id+"F0.wireOp",EDGE,"E9")])]});
            var Q1;
            Q1=makeQuery(id+"F16.opChamfer","BLEND_FACE",FACE,{"disambiguationData":[OSD([sQuery(id+"F0.wireOp",EDGE,"E5.MirrorCS"),sQuery(id+"F0.wireOp",EDGE,"E10")])]});
            fillet(context, id + "F17", {"entities" : qUnion([Q0, Q1]), "radius" : 1 * mm, "tangentPropagation" : true, "allowEdgeOverflow" : false});
        }
        {
            var Q0;
            Q0=makeQuery(id+"F2.imprint","IMPRINT",FACE,{"disambiguationData":[TD([[makeQuery(id+"F2.imprint","IMPRINT",EDGE,{"derivedFrom":sQuery(id+"F2.wireOp",EDGE,"E36.MirrorC")}),1.0]])]});
            var Q1;
            Q1=makeQuery(id+"F2.imprint","IMPRINT",FACE,{"disambiguationData":[TD([[makeQuery(id+"F2.imprint","IMPRINT",EDGE,{"derivedFrom":sQuery(id+"F2.wireOp",EDGE,"E34")}),-1.0]])]});
            extrude(context, id + "F18", {"entities" : qUnion([Q0, Q1]), "operationType" : NewBodyOperationType.REMOVE, "depth" : 25 * mm});
        }
    });
